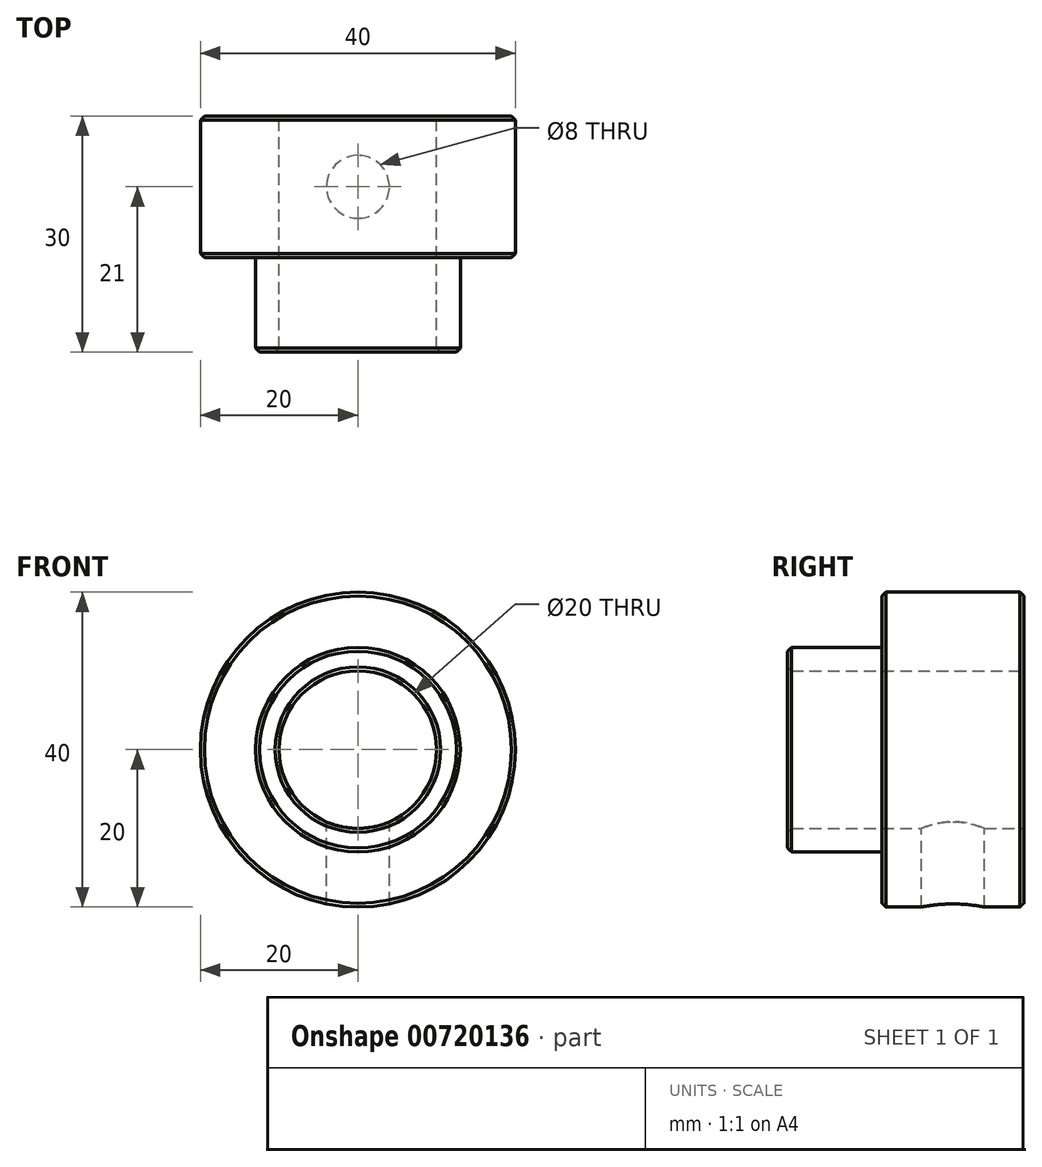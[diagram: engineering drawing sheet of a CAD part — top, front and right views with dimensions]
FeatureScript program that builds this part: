
annotation { "Feature Type Name" : "Feature", "Feature Type Description" : "" }
export const myFeature = defineFeature(function(context is Context, id is Id, definition is map)
    precondition{}
    {
        {
            var Q0;
            Q0=qCreatedBy(makeId("Front.planeOp"),FACE);
            var sketch = newSketch(context, id + "F0", { "sketchPlane" : qUnion([Q0])});
            skCircle(sketch, "E0", {"center": v(0, 0) * mm, "radius": 10 * mm});
            skCircle(sketch, "E1", {"center": v(0, 0) * mm, "radius": 20 * mm});
            skSolve(sketch);
        }
        {
            var Q0;
            Q0=makeQuery(id+"F0.imprint","IMPRINT",FACE,{"disambiguationData":[TD([[makeQuery(id+"F0.imprint","IMPRINT",EDGE,{"derivedFrom":sQuery(id+"F0.wireOp",EDGE,"E0")}),-1.0]])]});
            extrude(context, id + "F1", {"entities" : qUnion([Q0]), "depth" : 18 * mm, "offsetDistance" : 25 * mm});
        }
        {
            var Q0;
            Q0=qCreatedBy(makeId("Top.planeOp"),FACE);
            var sketch = newSketch(context, id + "F2", { "sketchPlane" : qUnion([Q0])});
            skCircle(sketch, "E2", {"center": v(0, -9) * mm, "radius": 4 * mm});
            skSolve(sketch);
        }
        {
            var Q0;
            Q0=makeQuery(id+"F2.imprint","IMPRINT",FACE,{"disambiguationData":[TD([[makeQuery(id+"F2.imprint","IMPRINT",EDGE,{"derivedFrom":sQuery(id+"F2.wireOp",EDGE,"E2")}),1.0]])]});
            extrude(context, id + "F3", {"entities" : qUnion([Q0]), "operationType" : NewBodyOperationType.REMOVE, "oppositeDirection" : true, "depth" : 25 * mm, "offsetDistance" : 25 * mm});
        }
        {
            var Q0;
            Q0=makeQuery(id+"F1.opExtrude","CAP_FACE",FACE,{"disambiguationData":[OSD([sQuery(id+"F0.wireOp",EDGE,"E0"),sQuery(id+"F0.wireOp",EDGE,"E1")])],"isStart":false});
            var sketch = newSketch(context, id + "F4", { "sketchPlane" : qUnion([Q0])});
            skCircle(sketch, "E3", {"center": v(0, 0) * mm, "radius": 10 * mm});
            skCircle(sketch, "E4", {"center": v(0, 0) * mm, "radius": 13 * mm});
            skSolve(sketch);
        }
        {
            var Q0;
            Q0=makeQuery(id+"F4.imprint","IMPRINT",FACE,{"disambiguationData":[TD([[makeQuery(id+"F4.imprint","IMPRINT",EDGE,{"derivedFrom":sQuery(id+"F4.wireOp",EDGE,"E3")}),-1.0]])]});
            extrude(context, id + "F5", {"entities" : qUnion([Q0]), "operationType" : NewBodyOperationType.ADD, "depth" : 12 * mm, "offsetDistance" : 25 * mm});
        }
        {
            var Q0;
            Q0=makeQuery(id+"F5.opExtrude","CAP_FACE",FACE,{"disambiguationData":[OSD([sQuery(id+"F4.wireOp",EDGE,"E3"),sQuery(id+"F4.wireOp",EDGE,"E4")])],"isStart":false});
            var Q1;
            Q1=makeQuery(id+"F5.opExtrude","CAP_EDGE",EDGE,{"disambiguationData":[OSD([sQuery(id+"F4.wireOp",EDGE,"E3")])],"isStart":false});
            var Q2;
            Q2=makeQuery(id+"F1.opExtrude","CAP_EDGE",EDGE,{"disambiguationData":[OSD([sQuery(id+"F0.wireOp",EDGE,"E1")])],"isStart":false});
            var Q3;
            Q3=makeQuery(id+"F1.opExtrude","CAP_EDGE",EDGE,{"disambiguationData":[OSD([sQuery(id+"F0.wireOp",EDGE,"E1")])],"isStart":true});
            chamfer(context, id + "F6", {"entities" : qUnion([Q0, Q1, Q2, Q3]), "width" : .5 * mm, "tangentPropagation" : true});
        }
    });
